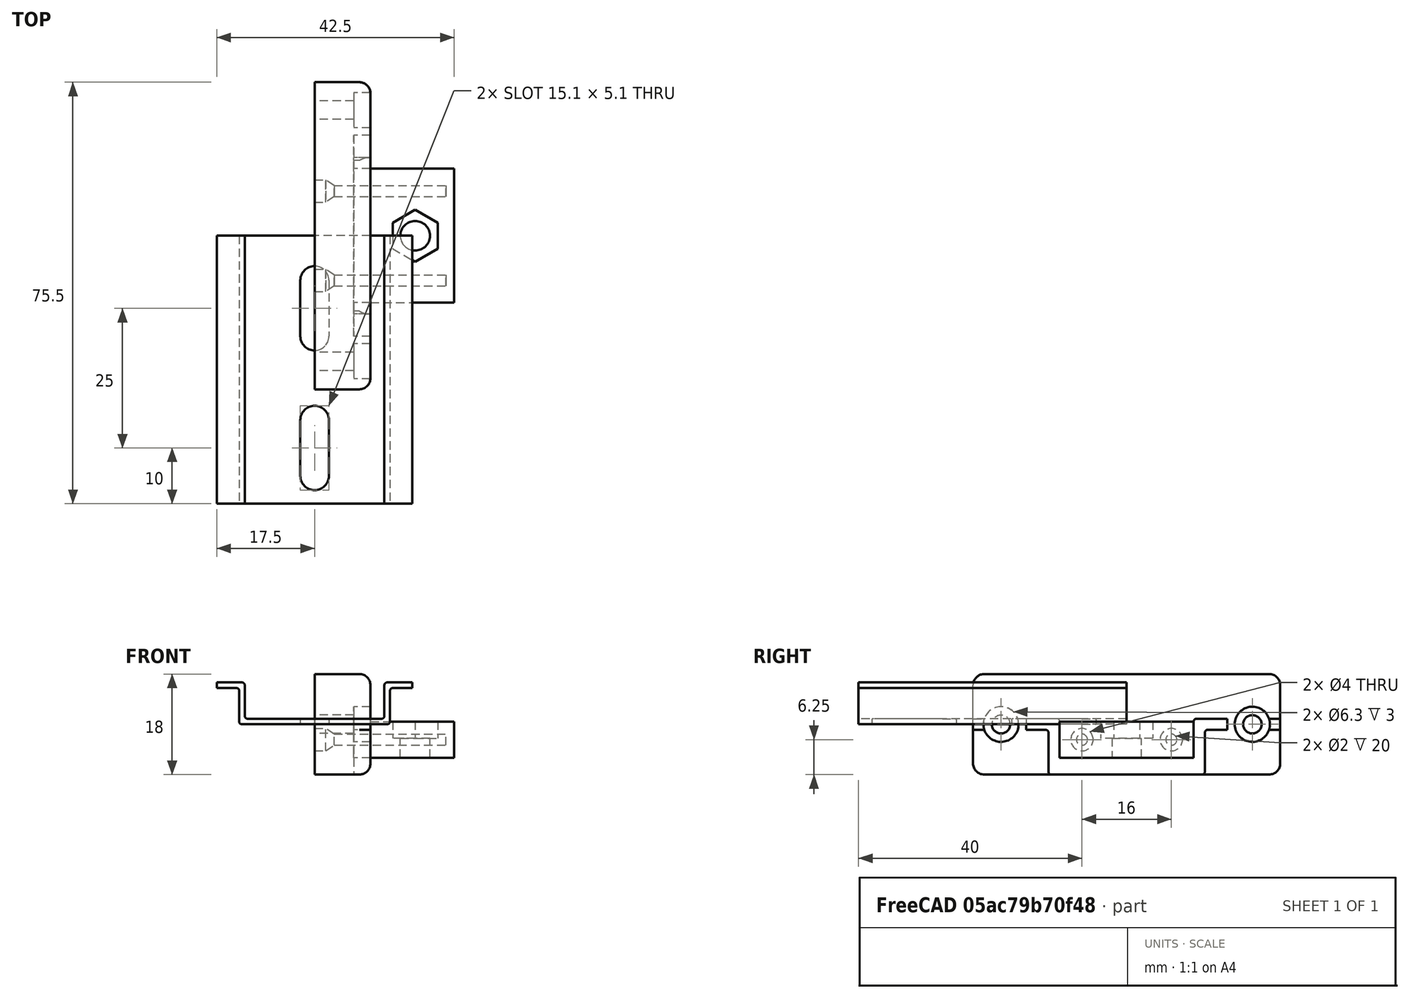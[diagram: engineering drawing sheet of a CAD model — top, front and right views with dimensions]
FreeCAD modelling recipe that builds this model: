
FCSTD DOCUMENT  (FreeCAD 0.18R)
Label: DIN-Rail-Holder
License: CreativeCommons Attribution
LicenseURL: http://creativecommons.org/licenses/by/4.0/
objects: Sketcher::SketchObject×9, PartDesign::Pocket×4, PartDesign::Pad×3, PartDesign::Body×3, App::Part×2, PartDesign::Hole×1, PartDesign::Fillet×1, PartDesign::Revolution×1, Spreadsheet::Sheet×1, Part::MultiCommon×1, PartDesign::FeatureBase×1, Part::Compound×1, Part::Cut×1, Mesh::Feature×1
note: 35 computed .brp shape members not serialized (recipe doc carries the construction recipe); baked Part::Feature solids carry a one-line shape summary decoded from their .brp

FEATURE [Sketcher::SketchObject] Sketch003  label="DIN-Rail-Shape"
  MapMode = 5
  Placement = pos=(10,-2e-15,2e-15) rot=(0.57735,0.57735,0.57735;2.0944rad)
  sketch-geometry (20):
    g0: LineSegment StartX=-18 StartY=-1 StartZ=0 EndX=-14.5 EndY=-1 EndZ=0
    g1: LineSegment StartX=-14 StartY=-1.5 StartZ=0 EndX=-14 EndY=-8.5 EndZ=0
    g2: LineSegment StartX=-13.5 StartY=-9 StartZ=0 EndX=13.5 EndY=-9 EndZ=0
    g3: LineSegment StartX=14 StartY=-8.5 StartZ=0 EndX=14 EndY=-1.5 EndZ=0
    g4: LineSegment StartX=14.5 StartY=-1 StartZ=0 EndX=18 EndY=-1 EndZ=0
    g5: ArcOfCircle CenterX=-14.5 CenterY=-1.5 CenterZ=0 NormalX=0 NormalY=0 NormalZ=1 AngleXU=0 Radius=0.5 StartAngle=1.032e-13 EndAngle=1.5708
    g6: ArcOfCircle CenterX=-13.5 CenterY=-8.5 CenterZ=0 NormalX=0 NormalY=0 NormalZ=1 AngleXU=0 Radius=0.5 StartAngle=3.14159 EndAngle=4.71239
    g7: ArcOfCircle CenterX=13.5 CenterY=-8.5 CenterZ=0 NormalX=0 NormalY=0 NormalZ=1 AngleXU=0 Radius=0.5 StartAngle=4.71239 EndAngle=6.28319
    g8: ArcOfCircle CenterX=14.5 CenterY=-1.5 CenterZ=0 NormalX=0 NormalY=0 NormalZ=1 AngleXU=0 Radius=0.5 StartAngle=1.5708 EndAngle=3.14159
    g9: LineSegment StartX=18 StartY=-1 StartZ=0 EndX=18 EndY=1 EndZ=0
    g10: LineSegment StartX=18 StartY=1 StartZ=0 EndX=12.5 EndY=1 EndZ=0
    g11: LineSegment StartX=12 StartY=0.5 StartZ=0 EndX=12 EndY=-5.5 EndZ=0
    g12: LineSegment StartX=11.5 StartY=-6 StartZ=0 EndX=-11.5 EndY=-6 EndZ=0
    g13: LineSegment StartX=-12 StartY=-5.5 StartZ=0 EndX=-12 EndY=0.5 EndZ=0
    g14: LineSegment StartX=-12.5 StartY=1 StartZ=0 EndX=-18 EndY=1 EndZ=0
    g15: LineSegment StartX=-18 StartY=1 StartZ=0 EndX=-18 EndY=-1 EndZ=0
    g16: ArcOfCircle CenterX=-12.5 CenterY=0.5 CenterZ=0 NormalX=0 NormalY=0 NormalZ=1 AngleXU=0 Radius=0.5 StartAngle=-1.03e-13 EndAngle=1.5708
    g17: ArcOfCircle CenterX=-11.5 CenterY=-5.5 CenterZ=0 NormalX=0 NormalY=0 NormalZ=1 AngleXU=0 Radius=0.5 StartAngle=3.14159 EndAngle=4.71239
    g18: ArcOfCircle CenterX=11.5 CenterY=-5.5 CenterZ=0 NormalX=0 NormalY=0 NormalZ=1 AngleXU=0 Radius=0.5 StartAngle=4.71239 EndAngle=6.28319
    g19: ArcOfCircle CenterX=12.5 CenterY=0.5 CenterZ=0 NormalX=0 NormalY=0 NormalZ=1 AngleXU=0 Radius=0.5 StartAngle=1.5708 EndAngle=3.14159
  constraints (50):
    c: Horizontal(g0)
    c: Vertical(g1)
    c: Vertical(g3)
    c: Horizontal(g4)
    c: Tangent(g0,g5) = 1.5708
    c: Tangent(g1,g5) = 1.5708
    c: Tangent(g1,g6) = -1.5708
    c: Tangent(g2,g6) = -1.5708
    c: Tangent(g2,g7) = -1.5708
    c: Tangent(g3,g7) = -1.5708
    c: Tangent(g3,g8) = 1.5708
    c: Tangent(g4,g8) = 1.5708
    c: Symmetric(g2,g2,g-2)
    c: DistanceX(g1,g3) = 28
    c: Vertical(g9)
    c: Coincident(g9,g10)
    c: Horizontal(g10)
    c: Vertical(g11)
    c: Vertical(g13)
    c: Horizontal(g14)
    c: Coincident(g14,g15)
    c: Coincident(g15,g0)
    c: Tangent(g14,g16) = -1.5708
    c: Tangent(g13,g16) = -1.5708
    c: Tangent(g13,g17) = 1.5708
    c: Tangent(g12,g17) = 1.5708
    c: Tangent(g12,g18) = 1.5708
    c: Tangent(g11,g18) = 1.5708
    c: Tangent(g11,g19) = -1.5708
    c: Tangent(g10,g19) = -1.5708
    c: Symmetric(g12,g12,g-2)
    c: Vertical(g15)
    c: DistanceX(g14,g9) = 36
    c: Coincident(g9,g4)
    c: Equal(g15,g9)
    c: DistanceY(g9,g9) = 2
    c: Equal(g5,g16)
    c: Equal(g16,g17)
    c: Equal(g17,g6)
    c: Equal(g6,g18)
    c: Equal(g18,g7)
    c: Equal(g7,g8)
    c: Equal(g8,g19)
    c: Equal(g1,g3)
    c: DistanceX(g11,g3) = 2
    c: Radius(g16) = 0.5
    c: Equal(g0,g4)
    c: DistanceY(g2,g9) = 10
    c: DistanceY(g2,g12) = 3
    c: DistanceY(g2,g-1) = 9
FEATURE [Sketcher::SketchObject] Sketch  label="BaseProfile"
  MapMode = 5
  Placement = pos=(0,0,0) rot=(0.57735,0.57735,0.57735;2.0944rad)
  sketch-geometry (8):
    g0: LineSegment StartX=25.5 StartY=-9 StartZ=0 EndX=-25.5 EndY=-9 EndZ=0
    g1: ArcOfCircle CenterX=-25.5 CenterY=-7 CenterZ=0 NormalX=0 NormalY=0 NormalZ=1 AngleXU=0 Radius=2 StartAngle=3.14159 EndAngle=4.71239
    g2: LineSegment StartX=-27.5 StartY=-7 StartZ=0 EndX=-27.5 EndY=7 EndZ=0
    g3: ArcOfCircle CenterX=-25.5 CenterY=7 CenterZ=0 NormalX=0 NormalY=0 NormalZ=1 AngleXU=0 Radius=2 StartAngle=1.5708 EndAngle=3.14159
    g4: LineSegment StartX=-25.5 StartY=9 StartZ=0 EndX=25.5 EndY=9 EndZ=0
    g5: ArcOfCircle CenterX=25.5 CenterY=7 CenterZ=0 NormalX=0 NormalY=0 NormalZ=1 AngleXU=0 Radius=2 StartAngle=3e-16 EndAngle=1.5708
    g6: LineSegment StartX=27.5 StartY=7 StartZ=0 EndX=27.5 EndY=-7 EndZ=0
    g7: ArcOfCircle CenterX=25.5 CenterY=-7 CenterZ=0 NormalX=0 NormalY=0 NormalZ=1 AngleXU=0 Radius=2 StartAngle=4.71239 EndAngle=6.28319
  constraints (18):
    c: Tangent(g0,g1) = 1.5708
    c: Tangent(g1,g2) = 1.5708
    c: Tangent(g2,g3) = 1.5708
    c: Tangent(g4,g5) = 1.5708
    c: Tangent(g5,g6) = 1.5708
    c: Horizontal(g4)
    c: Tangent(g0,g7) = 1.5708
    c: Tangent(g6,g7) = 1.5708
    c: Radius(g1) = 2
    c: Equal(g1,g3)
    c: Equal(g1,g5)
    c: Equal(g1,g7)
    c: Tangent(g3,g4) = 1.5708
    c: Vertical(g2)
    c: Symmetric(g0,g0,g-2)
    c: DistanceY(g0,g4) = 18
    c: DistanceX(g1,g6) = 55
    c: Symmetric(g0,g4,g-1)
FEATURE [Sketcher::SketchObject] Sketch004  label="TongueShape"
  MapMode = 5
  Placement = pos=(10,-2e-15,2e-15) rot=(0.57735,0.57735,0.57735;2.0944rad)
  sketch-geometry (4):
    g0: LineSegment StartX=-12 StartY=0.5 StartZ=0 EndX=12 EndY=0.5 EndZ=0
    g1: LineSegment StartX=12 StartY=0.5 StartZ=0 EndX=12 EndY=-6 EndZ=0
    g2: LineSegment StartX=12 StartY=-6 StartZ=0 EndX=-12 EndY=-6 EndZ=0
    g3: LineSegment StartX=-12 StartY=-6 StartZ=0 EndX=-12 EndY=0.5 EndZ=0
  constraints (11):
    c: Coincident(g0,g1)
    c: Coincident(g1,g2)
    c: Coincident(g2,g3)
    c: Coincident(g3,g0)
    c: Horizontal(g2)
    c: Vertical(g1)
    c: Vertical(g3)
    c: Symmetric(g0,g0,g-2)
    c: DistanceY(g1,g-1) = 6
    c: DistanceX(g0,g0) = 24
    c: DistanceY(g1,g1) = 6.5
FEATURE [Sketcher::SketchObject] Sketch006  label="M5HolePos"
  MapMode = 5
  Placement = pos=(0,0,0.5) rot=(0,0,-1;1.5708rad)
  sketch-geometry (1):
    g0: Circle CenterX=0 CenterY=18 CenterZ=0 NormalX=0 NormalY=0 NormalZ=1 AngleXU=0 Radius=2.65
  constraints (3):
    c: PointOnObject(g0,g-2)
    c: Radius(g0) = 2.65
    c: DistanceY(g-1,g0) = 18
FEATURE [Sketcher::SketchObject] Sketch007  label="M5NutShape"
  MapMode = 5
  Placement = pos=(0,0,0.5) rot=(0,0,-1;1.5708rad)
  sketch-geometry (7):
    g0: LineSegment StartX=-4.65 StartY=18 StartZ=0 EndX=-2.325 EndY=13.973 EndZ=0
    g1: LineSegment StartX=-2.325 StartY=13.973 StartZ=0 EndX=2.325 EndY=13.973 EndZ=0
    g2: LineSegment StartX=2.325 StartY=13.973 StartZ=0 EndX=4.65 EndY=18 EndZ=0
    g3: LineSegment StartX=4.65 StartY=18 StartZ=0 EndX=2.325 EndY=22.027 EndZ=0
    g4: LineSegment StartX=2.325 StartY=22.027 StartZ=0 EndX=-2.325 EndY=22.027 EndZ=0
    g5: LineSegment StartX=-2.325 StartY=22.027 StartZ=0 EndX=-4.65 EndY=18 EndZ=0
    g6: Circle [constr] CenterX=0 CenterY=18 CenterZ=0 NormalX=0 NormalY=0 NormalZ=1 AngleXU=0 Radius=4.65
  constraints (17):
    c: Coincident(g0,g1)
    c: Coincident(g1,g2)
    c: Coincident(g2,g3)
    c: Coincident(g3,g4)
    c: Coincident(g4,g5)
    c: Coincident(g5,g0)
    c: Equal(g0, g1-g5) x5
    c: PointOnObject(g0,g6)
    c: PointOnObject(g1,g6)
    c: PointOnObject(g2,g6)
    c: PointOnObject(g3,g6)
    c: PointOnObject(g4,g6)
    c: PointOnObject(g5,g6)
    c: DistanceY(g-1,g6) = 18
    c: PointOnObject(g6,g-2)
    c: Radius(g6) = 4.65
    c: Horizontal(g4)
FEATURE [PartDesign::Pad] Pad  label="Base"
  Length = 10
  Length2 = 100
  Placement = pos=(0,0,0) rot=(0.57735,0.57735,0.57735;2.0944rad)
  Profile = -> Sketch
  Type = 0
FEATURE [PartDesign::Pad] Pad001  label="Tongue"
  BaseFeature = -> Pad
  Length = 15
  Length2 = 100
  Placement = pos=(0,0,0) rot=(0.57735,0.57735,0.57735;2.0944rad)
  Profile = -> Sketch004
  Type = 0
FEATURE [PartDesign::Pocket] Pocket  label="RailCutout"
  BaseFeature = -> Pad001
  Length = 3
  Length2 = 100
  Placement = pos=(0,0,0) rot=(0.57735,0.57735,0.57735;2.0944rad)
  Profile = -> Sketch003
  Type = 0
FEATURE [Sketcher::SketchObject] Sketch005  label="ExtrusionScrewHolePos"
  MapMode = 5
  Placement = pos=(10,0,0) rot=(0.57735,0.57735,0.57735;2.0944rad)
  Support = -> [Pocket]
  sketch-geometry (2):
    g0: Circle CenterX=-22.5 CenterY=0 CenterZ=0 NormalX=0 NormalY=0 NormalZ=1 AngleXU=0 Radius=1.75
    g1: Circle CenterX=22.5 CenterY=0 CenterZ=0 NormalX=0 NormalY=0 NormalZ=1 AngleXU=0 Radius=1.75
  constraints (5):
    c: Radius(g0) = 1.75
    c: Equal(g0,g1)
    c: PointOnObject(g0,g-1)
    c: Symmetric(g0,g1,g-2)
    c: DistanceX(g0,g1) = 45
FEATURE [PartDesign::Hole] Hole  label="ExtrusionScrewHoles"
  BaseFeature = -> Pocket
  Depth = 25
  DepthType = 0
  Diameter = 3.3
  DrillPoint = 1
  DrillPointAngle = 118
  HoleCutCountersinkAngle = 90
  HoleCutDepth = 3
  HoleCutDiameter = 6.3
  HoleCutType = 1
  ModelActualThread = false
  Placement = pos=(0,0,0) rot=(0.57735,0.57735,0.57735;2.0944rad)
  Profile = -> Sketch005
  Tapered = false
  TaperedAngle = 90
  ThreadAngle = 0
  ThreadClass = 0
  ThreadCutOffInner = 0
  ThreadCutOffOuter = 0
  ThreadDirection = 0
  ThreadFit = 0
  ThreadPitch = 0
  ThreadSize = 0
  ThreadType = 0
  Threaded = false
FEATURE [PartDesign::Pocket] Pocket001  label="M5Hole"
  BaseFeature = -> Hole
  Length = 8
  Length2 = 100
  Placement = pos=(0,0,0) rot=(0.57735,0.57735,0.57735;2.0944rad)
  Profile = -> Sketch006
  Type = 0
FEATURE [PartDesign::Pocket] Pocket002  label="M5NutHole"
  BaseFeature = -> Pocket001
  Length = 3
  Length2 = 100
  Placement = pos=(0,0,0) rot=(0.57735,0.57735,0.57735;2.0944rad)
  Profile = -> Sketch007
  Type = 0
FEATURE [PartDesign::Fillet] Fillet
  Base = -> Pocket002 [Edge25]
  BaseFeature = -> Pocket002
  Placement = pos=(0,0,0) rot=(0.57735,0.57735,0.57735;2.0944rad)
  Radius = 2
FEATURE [PartDesign::Body] Body
  Group = -> [Pad,Sketch004,Pad001,Sketch003,Pocket,Sketch005,Hole,Sketch006,Pocket001,Sketch007,Pocket002,Fillet]
  Origin = -> Origin
  Tip = -> Fillet
FEATURE [Sketcher::SketchObject] Sketch008  label="M2x20HoleShape"
  MapMode = 5
  Placement = pos=(0,0,0) rot=(1,0,0;1.5708rad)
  Support = -> [XZ_Plane001]
  sketch-geometry (6):
    g0: LineSegment StartX=0 StartY=0 StartZ=0 EndX=0 EndY=-2 EndZ=0
    g1: LineSegment StartX=0 StartY=-2 StartZ=0 EndX=2 EndY=-2 EndZ=0
    g2: LineSegment StartX=2 StartY=-2 StartZ=0 EndX=3.5 EndY=-1 EndZ=0
    g3: LineSegment StartX=3.5 StartY=-1 StartZ=0 EndX=23.5 EndY=-1 EndZ=0
    g4: LineSegment StartX=23.5 StartY=-1 StartZ=0 EndX=23.5 EndY=0 EndZ=0
    g5: LineSegment StartX=23.5 StartY=0 StartZ=0 EndX=0 EndY=0 EndZ=0
  constraints (17):
    c: Coincident(g0,g1)
    c: Coincident(g1,g2)
    c: Coincident(g2,g3)
    c: Coincident(g3,g4)
    c: Coincident(g4,g5)
    c: Coincident(g5,g0)
    c: Coincident(g0,g-1)
    c: Horizontal(g5)
    c: Horizontal(g3)
    c: Horizontal(g1)
    c: Vertical(g0)
    c: Vertical(g4)
    c: DistanceY(g0,g0) = 2
    c: DistanceY(g4,g4) = 1
    c: DistanceX(g1,g2) = 1.5
    c: DistanceX(g1,g1) = 2
    c: DistanceX(g3,g3) = 20
FEATURE [PartDesign::Revolution] Revolution  label="M2x20-Hole"
  Angle = 360
  Axis = (1,0,0)
  Base = (0,0,0)
  Placement = pos=(0,0,0) rot=(1,0,0;1.5708rad)
  Profile = -> Sketch008
  ReferenceAxis = -> Sketch008 [H_Axis]
  Reversed = true
FEATURE [PartDesign::Body] Body001  label="StabilizerCutout"
  Group = -> [Sketch008,Revolution]
  Origin = -> Origin001
  Placement = pos=(0,-8,-2.75) rot=(0,0,1;0rad)
  Tip = -> Revolution
FEATURE [Sketcher::SketchObject] Sketch001
  MapMode = 5
  Placement = pos=(0,0,0) rot=(1,0,0;1.5708rad)
  sketch-geometry (20):
    g0: LineSegment StartX=-17.5 StartY=6.5 StartZ=0 EndX=-14 EndY=6.5 EndZ=0
    g1: LineSegment StartX=-13.5 StartY=6 StartZ=0 EndX=-13.5 EndY=0.5 EndZ=0
    g2: LineSegment StartX=-13 StartY=0 StartZ=0 EndX=13 EndY=0 EndZ=0
    g3: LineSegment StartX=13.5 StartY=0.5 StartZ=0 EndX=13.5 EndY=6 EndZ=0
    g4: LineSegment StartX=14 StartY=6.5 StartZ=0 EndX=17.5 EndY=6.5 EndZ=0
    g5: ArcOfCircle CenterX=-14 CenterY=6 CenterZ=0 NormalX=0 NormalY=0 NormalZ=1 AngleXU=0 Radius=0.5 StartAngle=0 EndAngle=1.5708
    g6: ArcOfCircle CenterX=-13 CenterY=0.5 CenterZ=0 NormalX=0 NormalY=0 NormalZ=1 AngleXU=0 Radius=0.5 StartAngle=3.14159 EndAngle=4.71239
    g7: ArcOfCircle CenterX=13 CenterY=0.5 CenterZ=0 NormalX=0 NormalY=0 NormalZ=1 AngleXU=0 Radius=0.5 StartAngle=4.71239 EndAngle=6.28319
    g8: ArcOfCircle CenterX=14 CenterY=6 CenterZ=0 NormalX=0 NormalY=0 NormalZ=1 AngleXU=0 Radius=0.5 StartAngle=1.5708 EndAngle=3.14159
    g9: LineSegment StartX=17.5 StartY=6.5 StartZ=0 EndX=17.5 EndY=7.5 EndZ=0
    g10: LineSegment StartX=17.5 StartY=7.5 StartZ=0 EndX=13 EndY=7.5 EndZ=0
    g11: LineSegment StartX=12.5 StartY=7 StartZ=0 EndX=12.5 EndY=1.5 EndZ=0
    g12: LineSegment StartX=12 StartY=1 StartZ=0 EndX=-12 EndY=1 EndZ=0
    g13: LineSegment StartX=-12.5 StartY=1.5 StartZ=0 EndX=-12.5 EndY=7 EndZ=0
    g14: LineSegment StartX=-13 StartY=7.5 StartZ=0 EndX=-17.5 EndY=7.5 EndZ=0
    g15: LineSegment StartX=-17.5 StartY=7.5 StartZ=0 EndX=-17.5 EndY=6.5 EndZ=0
    g16: ArcOfCircle CenterX=-13 CenterY=7 CenterZ=0 NormalX=0 NormalY=0 NormalZ=1 AngleXU=0 Radius=0.5 StartAngle=0 EndAngle=1.5708
    g17: ArcOfCircle CenterX=-12 CenterY=1.5 CenterZ=0 NormalX=0 NormalY=0 NormalZ=1 AngleXU=0 Radius=0.5 StartAngle=3.14159 EndAngle=4.71239
    g18: ArcOfCircle CenterX=12 CenterY=1.5 CenterZ=0 NormalX=0 NormalY=0 NormalZ=1 AngleXU=0 Radius=0.5 StartAngle=4.71239 EndAngle=6.28319
    g19: ArcOfCircle CenterX=13 CenterY=7 CenterZ=0 NormalX=0 NormalY=0 NormalZ=1 AngleXU=0 Radius=0.5 StartAngle=1.5708 EndAngle=3.14159
  constraints (50):
    c: Horizontal(g0)
    c: Vertical(g1)
    c: Vertical(g3)
    c: Horizontal(g4)
    c: Tangent(g0,g5) = 1.5708
    c: Tangent(g1,g5) = 1.5708
    c: Tangent(g1,g6) = -1.5708
    c: Tangent(g2,g6) = -1.5708
    c: Tangent(g2,g7) = -1.5708
    c: Tangent(g3,g7) = -1.5708
    c: Tangent(g3,g8) = 1.5708
    c: Tangent(g4,g8) = 1.5708
    c: PointOnObject(g2,g-1)
    c: Symmetric(g2,g2,g-2)
    c: DistanceX(g1,g3) = 27
    c: Vertical(g9)
    c: Coincident(g9,g10)
    c: Horizontal(g10)
    c: Vertical(g11)
    c: Vertical(g13)
    c: Horizontal(g14)
    c: Coincident(g14,g15)
    c: Coincident(g15,g0)
    c: Tangent(g14,g16) = -1.5708
    c: Tangent(g13,g16) = -1.5708
    c: Tangent(g13,g17) = 1.5708
    c: Tangent(g12,g17) = 1.5708
    c: Tangent(g12,g18) = 1.5708
    c: Tangent(g11,g18) = 1.5708
    c: Tangent(g11,g19) = -1.5708
    c: Tangent(g10,g19) = -1.5708
    c: Symmetric(g12,g12,g-2)
    c: Vertical(g15)
    c: DistanceY(g-1,g12) = 1
    c: DistanceY(g-1,g9) = 7.5
    c: DistanceX(g14,g9) = 35
    c: Coincident(g9,g4)
    c: Equal(g15,g9)
    c: DistanceY(g9,g9) = 1
    c: Equal(g5,g16)
    c: Equal(g16,g17)
    c: Equal(g17,g6)
    c: Equal(g6,g18)
    c: Equal(g18,g7)
    c: Equal(g7,g8)
    c: Equal(g8,g19)
    c: Equal(g1,g3)
    c: DistanceX(g11,g3) = 1
    c: Radius(g16) = 0.5
    c: Equal(g0,g4)
FEATURE [Spreadsheet::Sheet] Spreadsheet
  cells = A2=longitud; B2(longitud)=48; A3=; B3=
FEATURE [PartDesign::Pad] Pad002
  Length = 48
  Length2 = 100
  Placement = pos=(0,0,0) rot=(1,0,0;1.5708rad)
  Profile = -> Sketch001
  Type = 0
  expr: Length = Spreadsheet.longitud
FEATURE [Sketcher::SketchObject] Sketch002
  ExternalGeometry = -> [Pad002]
  MapMode = 5
  Placement = pos=(0,0,1) rot=(0,0,1;3.14159rad)
  Support = -> [Pad002]
  sketch-geometry (8):
    g0: ArcOfCircle CenterX=0 CenterY=33 CenterZ=0 NormalX=0 NormalY=0 NormalZ=1 AngleXU=0 Radius=2.55 StartAngle=3.14159 EndAngle=6.28319
    g1: ArcOfCircle CenterX=-1e-16 CenterY=43 CenterZ=0 NormalX=0 NormalY=0 NormalZ=1 AngleXU=0 Radius=2.55 StartAngle=8e-16 EndAngle=3.14159
    g2: LineSegment StartX=2.55 StartY=33 StartZ=0 EndX=2.55 EndY=43 EndZ=0
    g3: LineSegment StartX=-2.55 StartY=33 StartZ=0 EndX=-2.55 EndY=43 EndZ=0
    g4: ArcOfCircle CenterX=-2e-16 CenterY=8 CenterZ=0 NormalX=0 NormalY=0 NormalZ=1 AngleXU=0 Radius=2.55 StartAngle=3.14159 EndAngle=6.28319
    g5: ArcOfCircle CenterX=0 CenterY=18 CenterZ=0 NormalX=0 NormalY=0 NormalZ=1 AngleXU=0 Radius=2.55 StartAngle=0 EndAngle=3.14159
    g6: LineSegment StartX=2.55 StartY=8 StartZ=0 EndX=2.55 EndY=18 EndZ=0
    g7: LineSegment StartX=-2.55 StartY=8 StartZ=0 EndX=-2.55 EndY=18 EndZ=0
  constraints (20):
    c: Tangent(g0,g3) = 1.5708
    c: Tangent(g0,g2) = -1.5708
    c: Tangent(g2,g1) = -1.5708
    c: Tangent(g3,g1) = 1.5708
    c: Vertical(g2)
    c: Tangent(g4,g7) = 1.5708
    c: Tangent(g4,g6) = -1.5708
    c: Tangent(g6,g5) = -1.5708
    c: Tangent(g7,g5) = 1.5708
    c: Vertical(g6)
    c: Equal(g4,g5)
    c: Equal(g0,g5)
    c: Equal(g5,g1)
    c: Radius(g1) = 2.55
    c: DistanceY(g0,g1) = 10
    c: DistanceY(g5,g1) = 25
    c: DistanceY(g4,g5) = 10
    c: PointOnObject(g0,g-2)
    c: PointOnObject(g5,g-2)
    c: DistanceY(g1,g-3) = 5
FEATURE [PartDesign::Pocket] Pocket003
  Length = 5
  Length2 = 100
  Placement = pos=(0,0,0) rot=(1,0,0;1.5708rad)
  Profile = -> Sketch002
  Type = 0
FEATURE [Part::MultiCommon] Common
  Shapes = -> [Pocket003,Pad002]
FEATURE [App::Part] Part001  label="TS35-Din-Rail"
  Group = -> [Pad002,Pocket003,Common,Sketch001,Sketch002,Spreadsheet]
  Origin = -> Origin003
  Placement = pos=(55,-1.22e-14,-7) rot=(0,0,1;4.71239rad)
FEATURE [PartDesign::FeatureBase] Clone
  BaseFeature = -> Body001
  Placement = pos=(0,-8,-2.75) rot=(0,0,1;0rad)
FEATURE [PartDesign::Body] Body002
  BaseFeature = -> Body001
  Group = -> [Clone]
  Origin = -> Origin004
  Placement = pos=(0,16,0) rot=(0,0,1;0rad)
  Tip = -> Clone
FEATURE [Part::Compound] Compound  label="Reinforcement"
  Links = -> [Body001,Body002]
FEATURE [Part::Cut] Cut  label="DIN-Rail-Holder"
  Base = -> Body
  Tool = -> Compound
FEATURE [App::Part] Part  label="DIN-Rail-Fastener"
  Group = -> [Body,Compound,Body001,Cut]
  Origin = -> Origin002
FEATURE [Mesh::Feature] Mesh  label="DIN-Rail-Holder (Meshed)"
  Placement = pos=(0,0,0) rot=(0,1,0;4.71239rad)
